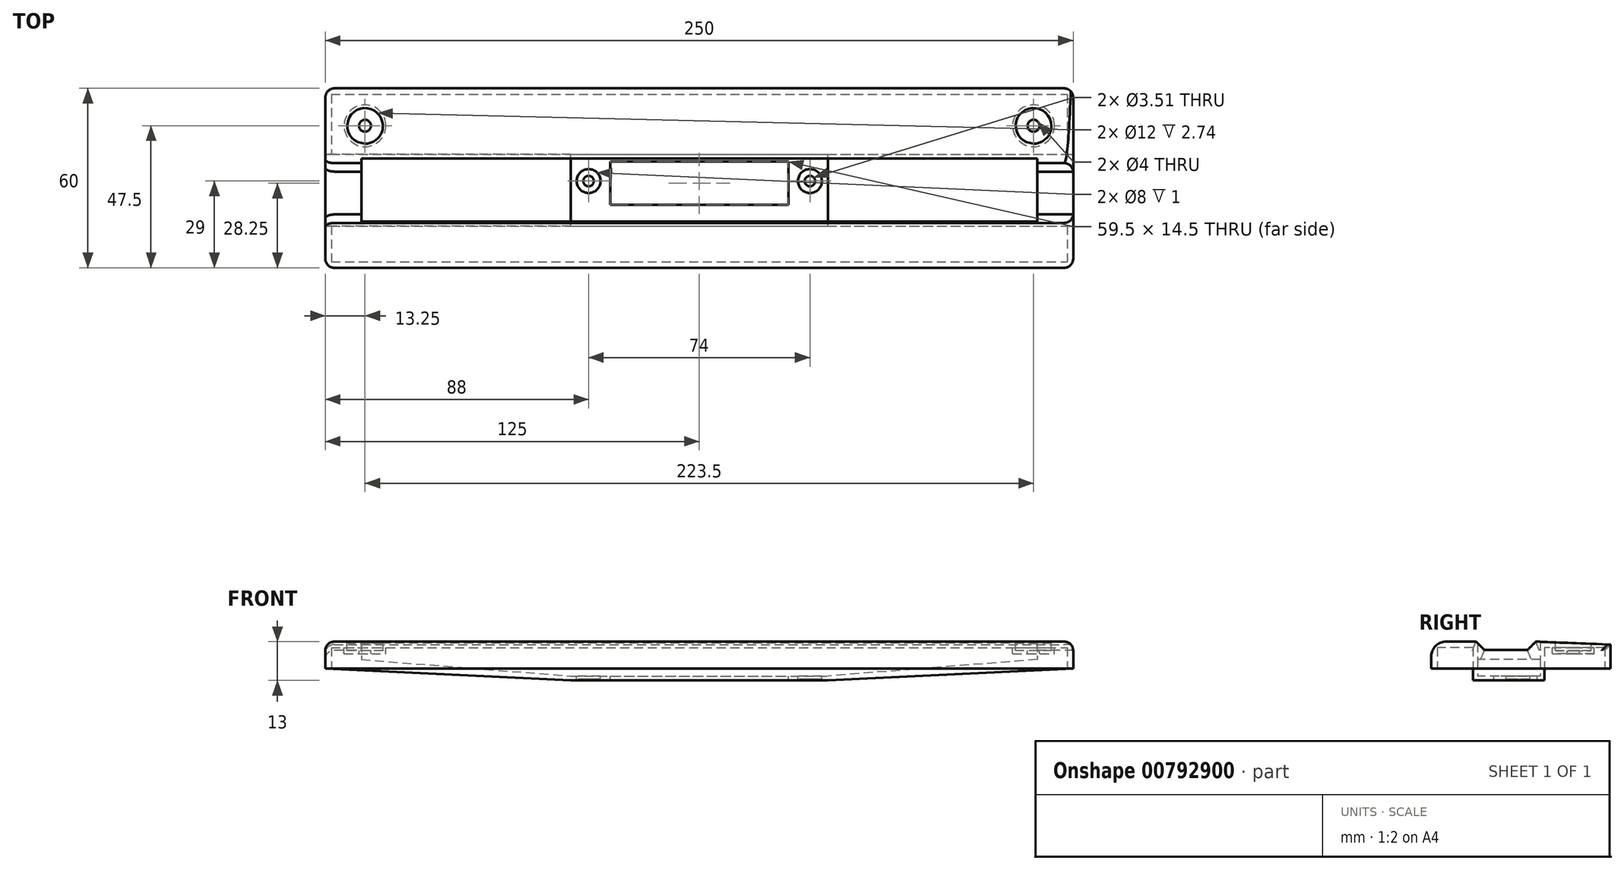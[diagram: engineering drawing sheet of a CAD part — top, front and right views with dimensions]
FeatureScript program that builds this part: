
annotation { "Feature Type Name" : "Feature", "Feature Type Description" : "" }
export const myFeature = defineFeature(function(context is Context, id is Id, definition is map)
    precondition{}
    {
        {
            var Q0;
            Q0=qCreatedBy(makeId("Top.planeOp"),FACE);
            var sketch = newSketch(context, id + "F0", { "sketchPlane" : qUnion([Q0])});
            skLineSegment(sketch, "E0.bottom", {"start": v(-125, 30) * mm, "end": v(125, 30) * mm});
            skLineSegment(sketch, "E0.top", {"start": v(-125, -30) * mm, "end": v(125, -30) * mm});
            skLineSegment(sketch, "E0.left", {"start": v(-125, 30) * mm, "end": v(-125, -30) * mm});
            skLineSegment(sketch, "E0.right", {"start": v(125, 30) * mm, "end": v(125, -30) * mm});
            skSolve(sketch);
        }
        {
            var Q0;
            Q0=makeQuery(id+"F0.imprint","IMPRINT",FACE,{"disambiguationData":[TD([[makeQuery(id+"F0.imprint","IMPRINT",EDGE,{"derivedFrom":sQuery(id+"F0.wireOp",EDGE,"E0.bottom")}),-1.0]])]});
            extrude(context, id + "F1", {"entities" : qUnion([Q0]), "depth" : 9 * mm, "offsetDistance" : 25 * mm});
        }
        {
            var Q0;
            Q0=qCreatedBy(makeId("Front.planeOp"),FACE);
            var sketch = newSketch(context, id + "F2", { "sketchPlane" : qUnion([Q0])});
            skLineSegment(sketch, "E1", {"start": v(-125, 0) * mm, "end": v(-43, 0) * mm});
            skLineSegment(sketch, "E2", {"start": v(-43, 0) * mm, "end": v(-43, -4) * mm});
            skLineSegment(sketch, "E3", {"start": v(-43, -4) * mm, "end": v(-125, 0) * mm});
            skLineSegment(sketch, "E4.MirrorCS", {"start": v(43, -4) * mm, "end": v(125, 0) * mm});
            skLineSegment(sketch, "E5.MirrorCS", {"start": v(43, 0) * mm, "end": v(43, -4) * mm});
            skLineSegment(sketch, "E6.MirrorCS", {"start": v(125, 0) * mm, "end": v(43, 0) * mm});
            skLineSegment(sketch, "E7", {"start": v(-43, -4) * mm, "end": v(43, -4) * mm});
            skLineSegment(sketch, "E8", {"start": v(-43, 0) * mm, "end": v(43, 0) * mm});
            skSolve(sketch);
        }
        {
            var Q0;
            Q0 = qSketchRegion(id + "F2", true);
            extrude(context, id + "F3", {"entities" : qUnion([Q0]), "operationType" : NewBodyOperationType.ADD, "depth" : 16 * mm, "offsetDistance" : 25 * mm});
        }
        {
            var Q0;
            Q0 = qSketchRegion(id + "F2", true);
            extrude(context, id + "F4", {"entities" : qUnion([Q0]), "operationType" : NewBodyOperationType.ADD, "oppositeDirection" : true, "depth" : 7.9 * mm, "offsetDistance" : 25 * mm});
        }
        {
            var Q0;
            Q0=makeQuery(id+"F1.opExtrude","CAP_FACE",FACE,{"disambiguationData":[OSD([sQuery(id+"F0.wireOp",EDGE,"E0.bottom"),sQuery(id+"F0.wireOp",EDGE,"E0.top"),sQuery(id+"F0.wireOp",EDGE,"E0.left"),sQuery(id+"F0.wireOp",EDGE,"E0.right")])],"isStart":false});
            var sketch = newSketch(context, id + "F5", { "sketchPlane" : qUnion([Q0])});
            skLineSegment(sketch, "E9.bottom", {"start": v(29.75, -9) * mm, "end": v(-29.75, -9) * mm});
            skLineSegment(sketch, "E9.top", {"start": v(29.75, 5.5) * mm, "end": v(-29.75, 5.5) * mm});
            skLineSegment(sketch, "E9.left", {"start": v(29.75, -9) * mm, "end": v(29.75, 5.5) * mm});
            skLineSegment(sketch, "E9.right", {"start": v(-29.75, -9) * mm, "end": v(-29.75, 5.5) * mm});
            skSolve(sketch);
        }
        {
            var Q0;
            Q0 = qSketchRegion(id + "F5", true);
            extrude(context, id + "F6", {"entities" : qUnion([Q0]), "operationType" : NewBodyOperationType.REMOVE, "endBound" : BoundingType.THROUGH_ALL, "oppositeDirection" : true, "depth" : 25 * mm, "offsetDistance" : 25 * mm});
        }
        {
            var Q0;
            {var subQ0=sQuery(id+"F2.wireOp",EDGE,"E7");Q0=makeQuery(id+"F4.boolean.opBoolean","MERGE",FACE,{"derivedFrom":[makeQuery(id+"F3.opExtrude","SWEPT_FACE",FACE,{"disambiguationData":[OSD([subQ0])]}),makeQuery(id+"F4.opExtrude","SWEPT_FACE",FACE,{"disambiguationData":[OSD([subQ0])]})]});}
            var sketch = newSketch(context, id + "F7", { "sketchPlane" : qUnion([Q0])});
            skCircle(sketch, "E10", {"center": v(-37, 1) * mm, "radius": 1.75 * mm});
            skLineSegment(sketch, "E11", {"start": v(0, 16) * mm, "end": v(0, -7.9) * mm});
            skCircle(sketch, "E12.MirrorC", {"center": v(37, 1) * mm, "radius": 1.75 * mm});
            skSolve(sketch);
        }
        {
            var Q0;
            Q0 = qSketchRegion(id + "F7", true);
            extrude(context, id + "F8", {"entities" : qUnion([Q0]), "operationType" : NewBodyOperationType.REMOVE, "endBound" : BoundingType.THROUGH_ALL, "oppositeDirection" : true, "depth" : 25 * mm, "offsetDistance" : 25 * mm});
        }
        {
            var Q0;
            {var subQ2=sQuery(id+"F0.wireOp",EDGE,"E0.right");var subQ3=sQuery(id+"F0.wireOp",EDGE,"E0.left");var subQ4=sQuery(id+"F0.wireOp",EDGE,"E0.bottom");Q0=makeQuery(id+"F3.boolean.opBoolean","SPLIT",FACE,{"disambiguationData":[TD([makeQuery(id+"F1.opExtrude","SWEPT_FACE",FACE,{"disambiguationData":[OSD([subQ4])]})])],"derivedFrom":makeQuery(id+"F1.opExtrude","CAP_FACE",FACE,{"disambiguationData":[OSD([subQ4,sQuery(id+"F0.wireOp",EDGE,"E0.top"),subQ3,subQ2])],"isStart":true})});}
            var sketch = newSketch(context, id + "F9", { "sketchPlane" : qUnion([Q0])});
            skLineSegment(sketch, "E13.bottom", {"start": v(-123, -28) * mm, "end": v(125, -28) * mm});
            skLineSegment(sketch, "E13.top", {"start": v(-123, -7.9) * mm, "end": v(123, -7.9) * mm});
            skLineSegment(sketch, "E13.left", {"start": v(-123, -28) * mm, "end": v(-123, -7.9) * mm});
            skLineSegment(sketch, "E13.right", {"start": v(123, -28) * mm, "end": v(123, -7.9) * mm});
            skLineSegment(sketch, "E14.bottom", {"start": v(-123, 16) * mm, "end": v(123, 16) * mm});
            skLineSegment(sketch, "E14.top", {"start": v(-123, 28) * mm, "end": v(123, 28) * mm});
            skLineSegment(sketch, "E14.left", {"start": v(-123, 16) * mm, "end": v(-123, 28) * mm});
            skLineSegment(sketch, "E14.right", {"start": v(123, 16) * mm, "end": v(123, 28) * mm});
            skSolve(sketch);
        }
        {
            var Q0;
            Q0 = qSketchRegion(id + "F9", true);
            extrude(context, id + "F10", {"entities" : qUnion([Q0]), "operationType" : NewBodyOperationType.REMOVE, "oppositeDirection" : true, "depth" : 7 * mm, "offsetDistance" : 25 * mm});
        }
        {
            var Q0;
            Q0=makeQuery(id+"F10.boolean.opBoolean","COPY",FACE,{"derivedFrom":makeQuery(id+"F10.opExtrude","CAP_FACE",FACE,{"disambiguationData":[OSD([sQuery(id+"F9.wireOp",EDGE,"E13.bottom"),sQuery(id+"F9.wireOp",EDGE,"E13.top"),sQuery(id+"F9.wireOp",EDGE,"E13.left"),sQuery(id+"F9.wireOp",EDGE,"E13.right")])],"isStart":false})});
            var sketch = newSketch(context, id + "F11", { "sketchPlane" : qUnion([Q0])});
            skCircle(sketch, "E15", {"center": v(-111.75, -17.5) * mm, "radius": 1.9 * mm});
            skCircle(sketch, "E16.MirrorC", {"center": v(111.75, -17.5) * mm, "radius": 1.9 * mm});
            skSolve(sketch);
        }
        {
            var Q0;
            Q0 = qSketchRegion(id + "F11", true);
            extrude(context, id + "F12", {"entities" : qUnion([Q0]), "operationType" : NewBodyOperationType.REMOVE, "endBound" : BoundingType.THROUGH_ALL, "oppositeDirection" : true, "depth" : 25 * mm, "offsetDistance" : 25 * mm});
        }
        {
            var Q0;
            Q0=makeQuery(id+"F1.opExtrude","CAP_FACE",FACE,{"disambiguationData":[OSD([sQuery(id+"F0.wireOp",EDGE,"E0.bottom"),sQuery(id+"F0.wireOp",EDGE,"E0.top"),sQuery(id+"F0.wireOp",EDGE,"E0.left"),sQuery(id+"F0.wireOp",EDGE,"E0.right")])],"isStart":false});
            var sketch = newSketch(context, id + "F13", { "sketchPlane" : qUnion([Q0])});
            skCircle(sketch, "E17", {"center": v(-111.75, 17.5) * mm, "radius": 6 * mm});
            skCircle(sketch, "E18", {"center": v(111.75, 17.5) * mm, "radius": 6 * mm});
            skSolve(sketch);
        }
        {
            var Q0;
            Q0=makeQuery(id+"F10.boolean.opBoolean","COPY",FACE,{"derivedFrom":makeQuery(id+"F10.opExtrude","CAP_FACE",FACE,{"disambiguationData":[OSD([sQuery(id+"F9.wireOp",EDGE,"E13.bottom"),sQuery(id+"F9.wireOp",EDGE,"E13.top"),sQuery(id+"F9.wireOp",EDGE,"E13.left"),sQuery(id+"F9.wireOp",EDGE,"E13.right")])],"isStart":false})});
            var sketch = newSketch(context, id + "F14", { "sketchPlane" : qUnion([Q0])});
            skCircle(sketch, "E19", {"center": v(-111.75, -17.5) * mm, "radius": 7 * mm});
            skCircle(sketch, "E20.MirrorC", {"center": v(111.75, -17.5) * mm, "radius": 7 * mm});
            skSolve(sketch);
        }
        {
            var Q0;
            Q0 = qSketchRegion(id + "F14", true);
            extrude(context, id + "F15", {"entities" : qUnion([Q0]), "operationType" : NewBodyOperationType.ADD, "depth" : 2 * mm, "offsetDistance" : 25 * mm});
        }
        {
            var Q0;
            Q0 = qSketchRegion(id + "F13", true);
            extrude(context, id + "F16", {"entities" : qUnion([Q0]), "operationType" : NewBodyOperationType.REMOVE, "oppositeDirection" : true, "depth" : 3 * mm, "offsetDistance" : 25 * mm});
        }
        {
            var Q0;
            Q0=makeQuery(id+"F16.boolean.opBoolean","COPY",FACE,{"derivedFrom":makeQuery(id+"F16.opExtrude","CAP_FACE",FACE,{"disambiguationData":[OSD([sQuery(id+"F13.wireOp",EDGE,"E18")])],"isStart":false})});
            var sketch = newSketch(context, id + "F17", { "sketchPlane" : qUnion([Q0])});
            skCircle(sketch, "E21", {"center": v(111.75, 17.5) * mm, "radius": 2 * mm});
            skCircle(sketch, "E22.MirrorC", {"center": v(-111.75, 17.5) * mm, "radius": 2 * mm});
            skSolve(sketch);
        }
        {
            var Q0;
            Q0 = qSketchRegion(id + "F17", true);
            extrude(context, id + "F18", {"entities" : qUnion([Q0]), "operationType" : NewBodyOperationType.REMOVE, "oppositeDirection" : true, "depth" : 25 * mm, "offsetDistance" : 25 * mm});
        }
        {
            var Q0;
            Q0=makeQuery(id+"F1.opExtrude","CAP_FACE",FACE,{"disambiguationData":[OSD([sQuery(id+"F0.wireOp",EDGE,"E0.bottom"),sQuery(id+"F0.wireOp",EDGE,"E0.top"),sQuery(id+"F0.wireOp",EDGE,"E0.left"),sQuery(id+"F0.wireOp",EDGE,"E0.right")])],"isStart":false});
            var sketch = newSketch(context, id + "F19", { "sketchPlane" : qUnion([Q0])});
            skLineSegment(sketch, "E23", {"start": v(-125, -14.5) * mm, "end": v(125, -14.5) * mm});
            skLineSegment(sketch, "E24", {"start": v(-125, 6.5) * mm, "end": v(125, 6.5) * mm});
            skLineSegment(sketch, "E25", {"start": v(-43, 6.5) * mm, "end": v(-43, -14.5) * mm});
            skLineSegment(sketch, "E26.MirrorCS", {"start": v(43, 6.5) * mm, "end": v(43, -14.5) * mm});
            skSolve(sketch);
        }
        {
            var Q0;
            Q0 = qSketchRegion(id + "F19", true);
            extrude(context, id + "F20", {"entities" : qUnion([Q0]), "operationType" : NewBodyOperationType.REMOVE, "oppositeDirection" : true, "depth" : 11.5 * mm, "offsetDistance" : 25 * mm});
        }
        {
            var Q0;
            Q0=makeQuery(id+"F20.boolean.opBoolean","COPY",FACE,{"derivedFrom":makeQuery(id+"F20.opExtrude","SWEPT_FACE",FACE,{"disambiguationData":[OSD([sQuery(id+"F19.wireOp",EDGE,"E23")])]})});
            var sketch = newSketch(context, id + "F21", { "sketchPlane" : qUnion([Q0])});
            skLineSegment(sketch, "E27", {"start": v(43, 9) * mm, "end": v(43, -2.5) * mm});
            skLineSegment(sketch, "E28", {"start": v(43, 9) * mm, "end": v(113, 9) * mm});
            skLineSegment(sketch, "E29", {"start": v(113, 9) * mm, "end": v(113, 3) * mm});
            skLineSegment(sketch, "E30", {"start": v(113, 3) * mm, "end": v(43, -2.5) * mm});
            skLineSegment(sketch, "E31.MirrorCS", {"start": v(-43, 9) * mm, "end": v(-113, 9) * mm});
            skLineSegment(sketch, "E32.MirrorCS", {"start": v(-113, 9) * mm, "end": v(-113, 3) * mm});
            skLineSegment(sketch, "E33.MirrorCS", {"start": v(-113, 3) * mm, "end": v(-43, -2.5) * mm});
            skLineSegment(sketch, "E34.MirrorCS", {"start": v(-43, 9) * mm, "end": v(-43, -2.5) * mm});
            skSolve(sketch);
        }
        {
            var Q0;
            Q0 = qSketchRegion(id + "F21", true);
            extrude(context, id + "F22", {"entities" : qUnion([Q0]), "operationType" : NewBodyOperationType.REMOVE, "depth" : 21 * mm, "offsetDistance" : 25 * mm});
        }
        {
            var Q0;
            Q0=makeQuery(id+"F1.opExtrude","SWEPT_FACE",FACE,{"disambiguationData":[OSD([sQuery(id+"F0.wireOp",EDGE,"E0.right")])]});
            var sketch = newSketch(context, id + "F23", { "sketchPlane" : qUnion([Q0])});
            skLineSegment(sketch, "E35", {"start": v(30, 8) * mm, "end": v(5, 9) * mm});
            skLineSegment(sketch, "E36", {"start": v(5, 9) * mm, "end": v(2.17, 6.17) * mm});
            skLineSegment(sketch, "E37", {"start": v(2.17, 6.17) * mm, "end": v(-12.17, 6.17) * mm});
            skLineSegment(sketch, "E38", {"start": v(-12.17, 6.17) * mm, "end": v(-15, 9) * mm});
            skSolve(sketch);
        }
        {
            var Q0;
            Q0 = qSketchRegion(id + "F23", true);
            var Q1;
            {var subQ0=sQuery(id+"F23.wireOp",EDGE,"E36");Q1=makeQuery(id+"F23.imprint","IMPRINT",FACE,{"disambiguationData":[TD([[makeQuery(id+"F23.imprint","IMPRINT",EDGE,{"derivedFrom":subQ0}),-1.0]])]});}
            var Q2;
            {var subQ0=sQuery(id+"F23.wireOp",EDGE,"E35");Q2=makeQuery(id+"F23.imprint","IMPRINT",FACE,{"disambiguationData":[TD([[makeQuery(id+"F23.imprint","IMPRINT",EDGE,{"derivedFrom":subQ0}),-1.0]])]});}
            extrude(context, id + "F24", {"entities" : qUnion([Q0, Q1, Q2]), "operationType" : NewBodyOperationType.REMOVE, "endBound" : BoundingType.THROUGH_ALL, "oppositeDirection" : true, "depth" : 25 * mm, "offsetDistance" : 25 * mm});
        }
        {
            var Q0;
            {var subQ0=sQuery(id+"F0.wireOp",EDGE,"E0.bottom");var subQ1=sQuery(id+"F0.wireOp",EDGE,"E0.right");Q0=makeQuery(id+"F24.boolean.opBoolean","SPLIT",EDGE,{"disambiguationData":[TD([makeQuery(id+"F1.opExtrude","SWEPT_FACE",FACE,{"disambiguationData":[OSD([subQ0])]})])],"derivedFrom":makeQuery(id+"F1.opExtrude","CAP_EDGE",EDGE,{"disambiguationData":[OSD([subQ1])],"isStart":false})});}
            var Q1;
            Q1=makeQuery(id+"F1.opExtrude","CAP_EDGE",EDGE,{"disambiguationData":[OSD([sQuery(id+"F0.wireOp",EDGE,"E0.bottom")])],"isStart":false});
            var Q2;
            {var subQ0=sQuery(id+"F0.wireOp",EDGE,"E0.bottom");var subQ1=sQuery(id+"F0.wireOp",EDGE,"E0.left");Q2=makeQuery(id+"F24.boolean.opBoolean","SPLIT",EDGE,{"disambiguationData":[TD([makeQuery(id+"F1.opExtrude","SWEPT_FACE",FACE,{"disambiguationData":[OSD([subQ0])]})])],"derivedFrom":makeQuery(id+"F1.opExtrude","CAP_EDGE",EDGE,{"disambiguationData":[OSD([subQ1])],"isStart":false})});}
            var Q3;
            {var subQ0=sQuery(id+"F0.wireOp",EDGE,"E0.left");var subQ1=sQuery(id+"F0.wireOp",EDGE,"E0.top");Q3=makeQuery(id+"F24.boolean.opBoolean","SPLIT",EDGE,{"disambiguationData":[TD([makeQuery(id+"F1.opExtrude","SWEPT_FACE",FACE,{"disambiguationData":[OSD([subQ1])]})])],"derivedFrom":makeQuery(id+"F1.opExtrude","CAP_EDGE",EDGE,{"disambiguationData":[OSD([subQ0])],"isStart":false})});}
            var Q4;
            {var subQ0=sQuery(id+"F0.wireOp",EDGE,"E0.right");var subQ1=sQuery(id+"F0.wireOp",EDGE,"E0.top");Q4=makeQuery(id+"F24.boolean.opBoolean","SPLIT",EDGE,{"disambiguationData":[TD([makeQuery(id+"F1.opExtrude","SWEPT_FACE",FACE,{"disambiguationData":[OSD([subQ1])]})])],"derivedFrom":makeQuery(id+"F1.opExtrude","CAP_EDGE",EDGE,{"disambiguationData":[OSD([subQ0])],"isStart":false})});}
            var Q5;
            Q5=makeQuery(id+"F24.boolean.opBoolean","COPY",EDGE,{"derivedFrom":makeQuery(id+"F24.opExtrude","CAP_EDGE",EDGE,{"disambiguationData":[OSD([sQuery(id+"F23.wireOp",EDGE,"E38")])],"isStart":true})});
            var Q6;
            Q6=makeQuery(id+"F24.boolean.opBoolean","COPY",EDGE,{"derivedFrom":makeQuery(id+"F24.opExtrude","CAP_EDGE",EDGE,{"disambiguationData":[OSD([sQuery(id+"F23.wireOp",EDGE,"E37")])],"isStart":true})});
            var Q7;
            Q7=makeQuery(id+"F24.boolean.opBoolean","COPY",EDGE,{"derivedFrom":makeQuery(id+"F24.opExtrude","CAP_EDGE",EDGE,{"disambiguationData":[OSD([sQuery(id+"F23.wireOp",EDGE,"E36")])],"isStart":true})});
            var Q8;
            Q8=makeQuery(id+"F24.boolean.opBoolean","INTERSECT",EDGE,{"derivedFrom":[makeQuery(id+"F1.opExtrude","SWEPT_FACE",FACE,{"disambiguationData":[OSD([sQuery(id+"F0.wireOp",EDGE,"E0.left")])]}),makeQuery(id+"F24.opExtrude","SWEPT_FACE",FACE,{"disambiguationData":[OSD([sQuery(id+"F23.wireOp",EDGE,"E36")])]})]});
            var Q9;
            Q9=makeQuery(id+"F24.boolean.opBoolean","INTERSECT",EDGE,{"derivedFrom":[makeQuery(id+"F1.opExtrude","SWEPT_FACE",FACE,{"disambiguationData":[OSD([sQuery(id+"F0.wireOp",EDGE,"E0.left")])]}),makeQuery(id+"F24.opExtrude","SWEPT_FACE",FACE,{"disambiguationData":[OSD([sQuery(id+"F23.wireOp",EDGE,"E37")])]})]});
            var Q10;
            Q10=makeQuery(id+"F24.boolean.opBoolean","INTERSECT",EDGE,{"derivedFrom":[makeQuery(id+"F1.opExtrude","SWEPT_FACE",FACE,{"disambiguationData":[OSD([sQuery(id+"F0.wireOp",EDGE,"E0.left")])]}),makeQuery(id+"F24.opExtrude","SWEPT_FACE",FACE,{"disambiguationData":[OSD([sQuery(id+"F23.wireOp",EDGE,"E38")])]})]});
            var Q11;
            Q11=makeQuery(id+"F1.opExtrude","SWEPT_EDGE",EDGE,{"disambiguationData":[OSD([sQuery(id+"F0.wireOp",EDGE,"E0.bottom"),sQuery(id+"F0.wireOp",EDGE,"E0.left")])]});
            var Q12;
            Q12=makeQuery(id+"F1.opExtrude","SWEPT_EDGE",EDGE,{"disambiguationData":[OSD([sQuery(id+"F0.wireOp",EDGE,"E0.top"),sQuery(id+"F0.wireOp",EDGE,"E0.left")])]});
            var Q13;
            Q13=makeQuery(id+"F1.opExtrude","SWEPT_EDGE",EDGE,{"disambiguationData":[OSD([sQuery(id+"F0.wireOp",EDGE,"E0.top"),sQuery(id+"F0.wireOp",EDGE,"E0.right")])]});
            var Q14;
            Q14=makeQuery(id+"F1.opExtrude","SWEPT_EDGE",EDGE,{"disambiguationData":[OSD([sQuery(id+"F0.wireOp",EDGE,"E0.bottom"),sQuery(id+"F0.wireOp",EDGE,"E0.right")])]});
            var Q15;
            Q15=makeQuery(id+"F24.boolean.opBoolean","COPY",EDGE,{"derivedFrom":makeQuery(id+"F24.opExtrude","CAP_EDGE",EDGE,{"disambiguationData":[OSD([sQuery(id+"F23.wireOp",EDGE,"E35")])],"isStart":true})});
            var Q16;
            Q16=makeQuery(id+"F24.boolean.opBoolean","COPY",EDGE,{"derivedFrom":makeQuery(id+"F24.opExtrude","SWEPT_EDGE",EDGE,{"disambiguationData":[OSD([sQuery(id+"F0.wireOp",EDGE,"E0.bottom"),sQuery(id+"F0.wireOp",EDGE,"E0.right"),sQuery(id+"F23.wireOp",EDGE,"E35")])]})});
            var Q17;
            Q17=makeQuery(id+"F24.boolean.opBoolean","INTERSECT",EDGE,{"derivedFrom":[makeQuery(id+"F1.opExtrude","SWEPT_FACE",FACE,{"disambiguationData":[OSD([sQuery(id+"F0.wireOp",EDGE,"E0.left")])]}),makeQuery(id+"F24.opExtrude","SWEPT_FACE",FACE,{"disambiguationData":[OSD([sQuery(id+"F23.wireOp",EDGE,"E35")])]})]});
            fillet(context, id + "F25", {"entities" : qUnion([Q0, Q1, Q2, Q3, Q4, Q5, Q6, Q7, Q8, Q9, Q10, Q11, Q12, Q13, Q14, Q15, Q16, Q17]), "radius" : 3 * mm, "tangentPropagation" : true, "allowEdgeOverflow" : false});
        }
        {
            var Q0;
            Q0=makeQuery(id+"F1.opExtrude","CAP_EDGE",EDGE,{"disambiguationData":[OSD([sQuery(id+"F0.wireOp",EDGE,"E0.top")])],"isStart":false});
            fillet(context, id + "F26", {"entities" : qUnion([Q0]), "radius" : 5 * mm, "tangentPropagation" : true, "allowEdgeOverflow" : false});
        }
        {
            var Q0;
            Q0=makeQuery(id+"F20.boolean.opBoolean","COPY",FACE,{"derivedFrom":makeQuery(id+"F20.opExtrude","CAP_FACE",FACE,{"disambiguationData":[OSD([sQuery(id+"F19.wireOp",EDGE,"E23"),sQuery(id+"F19.wireOp",EDGE,"E24"),sQuery(id+"F19.wireOp",EDGE,"E25"),sQuery(id+"F19.wireOp",EDGE,"E26.MirrorCS")])],"isStart":false})});
            var sketch = newSketch(context, id + "F27", { "sketchPlane" : qUnion([Q0])});
            skCircle(sketch, "E39", {"center": v(37, -1) * mm, "radius": 4 * mm});
            skCircle(sketch, "E40.MirrorC", {"center": v(-37, -1) * mm, "radius": 4 * mm});
            skSolve(sketch);
        }
        {
            var Q0;
            Q0 = qSketchRegion(id + "F27", true);
            extrude(context, id + "F28", {"entities" : qUnion([Q0]), "operationType" : NewBodyOperationType.REMOVE, "oppositeDirection" : true, "depth" : 1 * mm, "offsetDistance" : 25 * mm});
        }
    });
